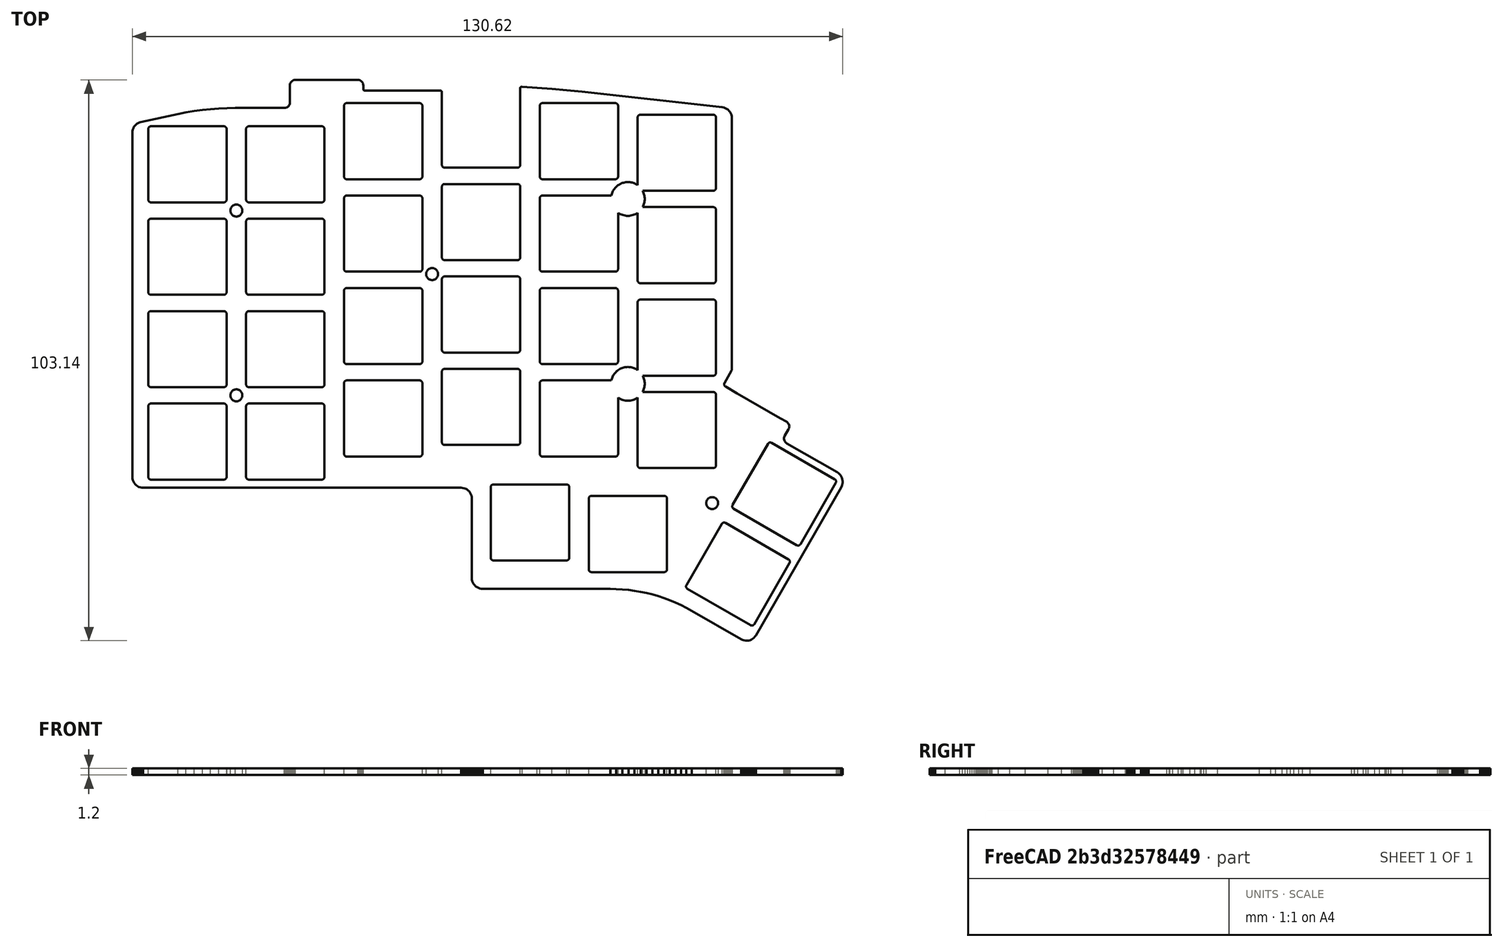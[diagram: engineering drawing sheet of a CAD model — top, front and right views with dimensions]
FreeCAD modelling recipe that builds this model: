
FCSTD DOCUMENT  (FreeCAD 0.19R)
Label: iris_case_extruded
License: All rights reserved
LicenseURL: http://en.wikipedia.org/wiki/All_rights_reserved
objects: Part::Feature×28, Part::Extrusion×28
note: 56 computed .brp shape members not serialized (recipe doc carries the construction recipe); baked Part::Feature solids carry a one-line shape summary decoded from their .brp

FEATURE [Part::Feature] Face
  shape: bbox 130.6 x 103.1 x 2e-07 mm, 1 faces, 0 solids (baked)
FEATURE [Part::Feature] Face001 .. Face004  x4 (patterned run collapsed; names and placements below)
  shape: bbox 2.2 x 2.2 x 2e-07 mm, 1 faces, 0 solids (baked)
FEATURE [Part::Feature] Face005
  shape: bbox 19.11 x 18.96 x 2e-07 mm, 1 faces, 0 solids (baked)
FEATURE [Part::Feature] Face006 .. Face015  x10 (patterned run collapsed; names and placements below)
  shape: bbox 14.4 x 14 x 2e-07 mm, 1 faces, 0 solids (baked)
FEATURE [Part::Feature] Face016
  shape: bbox 32.4 x 31 x 2e-07 mm, 1 faces, 0 solids (baked)
FEATURE [Part::Feature] Face017
  shape: bbox 14.4 x 14 x 2e-07 mm, 1 faces, 0 solids (baked)
FEATURE [Part::Feature] Face018
  shape: bbox 19.11 x 18.96 x 2e-07 mm, 1 faces, 0 solids (baked)
FEATURE [Part::Feature] Face019
  shape: bbox 14.4 x 14 x 2e-07 mm, 1 faces, 0 solids (baked)
FEATURE [Part::Feature] Face020
  shape: bbox 14.4 x 14 x 2e-07 mm, 1 faces, 0 solids (baked)
FEATURE [Part::Feature] Face021
  shape: bbox 14.4 x 14 x 2e-07 mm, 1 faces, 0 solids (baked)
FEATURE [Part::Feature] Face022
  shape: bbox 32.4 x 31 x 2e-07 mm, 1 faces, 0 solids (baked)
FEATURE [Part::Feature] Face023 .. Face027  x5 (patterned run collapsed; names and placements below)
  shape: bbox 14.4 x 14 x 2e-07 mm, 1 faces, 0 solids (baked)
FEATURE [Part::Extrusion] Extrude
  Base = -> Face
  Dir = (0,0,1)
  DirMode = 0
  FaceMakerClass = Part::FaceMakerBullseye
  LengthFwd = 1.2
  LengthRev = 0
  Solid = true
  Symmetric = false
FEATURE [Part::Extrusion] Extrude001
  Base = -> Face001
  Dir = (0,0,1)
  DirMode = 0
  FaceMakerClass = Part::FaceMakerBullseye
  LengthFwd = 1.2
  LengthRev = 0
  Solid = true
  Symmetric = false
FEATURE [Part::Extrusion] Extrude002
  Base = -> Face002
  Dir = (0,0,1)
  DirMode = 0
  FaceMakerClass = Part::FaceMakerBullseye
  LengthFwd = 1.2
  LengthRev = 0
  Solid = true
  Symmetric = false
FEATURE [Part::Extrusion] Extrude003
  Base = -> Face003
  Dir = (0,0,1)
  DirMode = 0
  FaceMakerClass = Part::FaceMakerBullseye
  LengthFwd = 1.2
  LengthRev = 0
  Solid = true
  Symmetric = false
FEATURE [Part::Extrusion] Extrude004
  Base = -> Face004
  Dir = (0,0,1)
  DirMode = 0
  FaceMakerClass = Part::FaceMakerBullseye
  LengthFwd = 1.2
  LengthRev = 0
  Solid = true
  Symmetric = false
FEATURE [Part::Extrusion] Extrude005
  Base = -> Face005
  Dir = (0,0,1)
  DirMode = 0
  FaceMakerClass = Part::FaceMakerBullseye
  LengthFwd = 1.2
  LengthRev = 0
  Solid = true
  Symmetric = false
FEATURE [Part::Extrusion] Extrude006
  Base = -> Face006
  Dir = (0,0,1)
  DirMode = 0
  FaceMakerClass = Part::FaceMakerBullseye
  LengthFwd = 1.2
  LengthRev = 0
  Solid = true
  Symmetric = false
FEATURE [Part::Extrusion] Extrude007
  Base = -> Face007
  Dir = (0,0,1)
  DirMode = 0
  FaceMakerClass = Part::FaceMakerBullseye
  LengthFwd = 1.2
  LengthRev = 0
  Solid = true
  Symmetric = false
FEATURE [Part::Extrusion] Extrude008
  Base = -> Face008
  Dir = (0,0,1)
  DirMode = 0
  FaceMakerClass = Part::FaceMakerBullseye
  LengthFwd = 1.2
  LengthRev = 0
  Solid = true
  Symmetric = false
FEATURE [Part::Extrusion] Extrude009
  Base = -> Face009
  Dir = (0,0,1)
  DirMode = 0
  FaceMakerClass = Part::FaceMakerBullseye
  LengthFwd = 1.2
  LengthRev = 0
  Solid = true
  Symmetric = false
FEATURE [Part::Extrusion] Extrude010
  Base = -> Face010
  Dir = (0,0,1)
  DirMode = 0
  FaceMakerClass = Part::FaceMakerBullseye
  LengthFwd = 1.2
  LengthRev = 0
  Solid = true
  Symmetric = false
FEATURE [Part::Extrusion] Extrude011
  Base = -> Face011
  Dir = (0,0,1)
  DirMode = 0
  FaceMakerClass = Part::FaceMakerBullseye
  LengthFwd = 1.2
  LengthRev = 0
  Solid = true
  Symmetric = false
FEATURE [Part::Extrusion] Extrude012
  Base = -> Face012
  Dir = (0,0,1)
  DirMode = 0
  FaceMakerClass = Part::FaceMakerBullseye
  LengthFwd = 1.2
  LengthRev = 0
  Solid = true
  Symmetric = false
FEATURE [Part::Extrusion] Extrude013
  Base = -> Face013
  Dir = (0,0,1)
  DirMode = 0
  FaceMakerClass = Part::FaceMakerBullseye
  LengthFwd = 1.2
  LengthRev = 0
  Solid = true
  Symmetric = false
FEATURE [Part::Extrusion] Extrude014
  Base = -> Face014
  Dir = (0,0,1)
  DirMode = 0
  FaceMakerClass = Part::FaceMakerBullseye
  LengthFwd = 1.2
  LengthRev = 0
  Solid = true
  Symmetric = false
FEATURE [Part::Extrusion] Extrude015
  Base = -> Face015
  Dir = (0,0,1)
  DirMode = 0
  FaceMakerClass = Part::FaceMakerBullseye
  LengthFwd = 1.2
  LengthRev = 0
  Solid = true
  Symmetric = false
FEATURE [Part::Extrusion] Extrude016
  Base = -> Face016
  Dir = (0,0,1)
  DirMode = 0
  FaceMakerClass = Part::FaceMakerBullseye
  LengthFwd = 1.2
  LengthRev = 0
  Solid = true
  Symmetric = false
FEATURE [Part::Extrusion] Extrude017
  Base = -> Face017
  Dir = (0,0,1)
  DirMode = 0
  FaceMakerClass = Part::FaceMakerBullseye
  LengthFwd = 1.2
  LengthRev = 0
  Solid = true
  Symmetric = false
FEATURE [Part::Extrusion] Extrude018
  Base = -> Face018
  Dir = (0,0,1)
  DirMode = 0
  FaceMakerClass = Part::FaceMakerBullseye
  LengthFwd = 1.2
  LengthRev = 0
  Solid = true
  Symmetric = false
FEATURE [Part::Extrusion] Extrude019
  Base = -> Face019
  Dir = (0,0,1)
  DirMode = 0
  FaceMakerClass = Part::FaceMakerBullseye
  LengthFwd = 1.2
  LengthRev = 0
  Solid = true
  Symmetric = false
FEATURE [Part::Extrusion] Extrude020
  Base = -> Face020
  Dir = (0,0,1)
  DirMode = 0
  FaceMakerClass = Part::FaceMakerBullseye
  LengthFwd = 1.2
  LengthRev = 0
  Solid = true
  Symmetric = false
FEATURE [Part::Extrusion] Extrude021
  Base = -> Face021
  Dir = (0,0,1)
  DirMode = 0
  FaceMakerClass = Part::FaceMakerBullseye
  LengthFwd = 1.2
  LengthRev = 0
  Solid = true
  Symmetric = false
FEATURE [Part::Extrusion] Extrude022
  Base = -> Face022
  Dir = (0,0,1)
  DirMode = 0
  FaceMakerClass = Part::FaceMakerBullseye
  LengthFwd = 1.2
  LengthRev = 0
  Solid = true
  Symmetric = false
FEATURE [Part::Extrusion] Extrude023
  Base = -> Face023
  Dir = (0,0,1)
  DirMode = 0
  FaceMakerClass = Part::FaceMakerBullseye
  LengthFwd = 1.2
  LengthRev = 0
  Solid = true
  Symmetric = false
FEATURE [Part::Extrusion] Extrude024
  Base = -> Face024
  Dir = (0,0,1)
  DirMode = 0
  FaceMakerClass = Part::FaceMakerBullseye
  LengthFwd = 1.2
  LengthRev = 0
  Solid = true
  Symmetric = false
FEATURE [Part::Extrusion] Extrude025
  Base = -> Face025
  Dir = (0,0,1)
  DirMode = 0
  FaceMakerClass = Part::FaceMakerBullseye
  LengthFwd = 1.2
  LengthRev = 0
  Solid = true
  Symmetric = false
FEATURE [Part::Extrusion] Extrude026
  Base = -> Face026
  Dir = (0,0,1)
  DirMode = 0
  FaceMakerClass = Part::FaceMakerBullseye
  LengthFwd = 1.2
  LengthRev = 0
  Solid = true
  Symmetric = false
FEATURE [Part::Extrusion] Extrude027
  Base = -> Face027
  Dir = (0,0,1)
  DirMode = 0
  FaceMakerClass = Part::FaceMakerBullseye
  LengthFwd = 1.2
  LengthRev = 0
  Solid = true
  Symmetric = false
